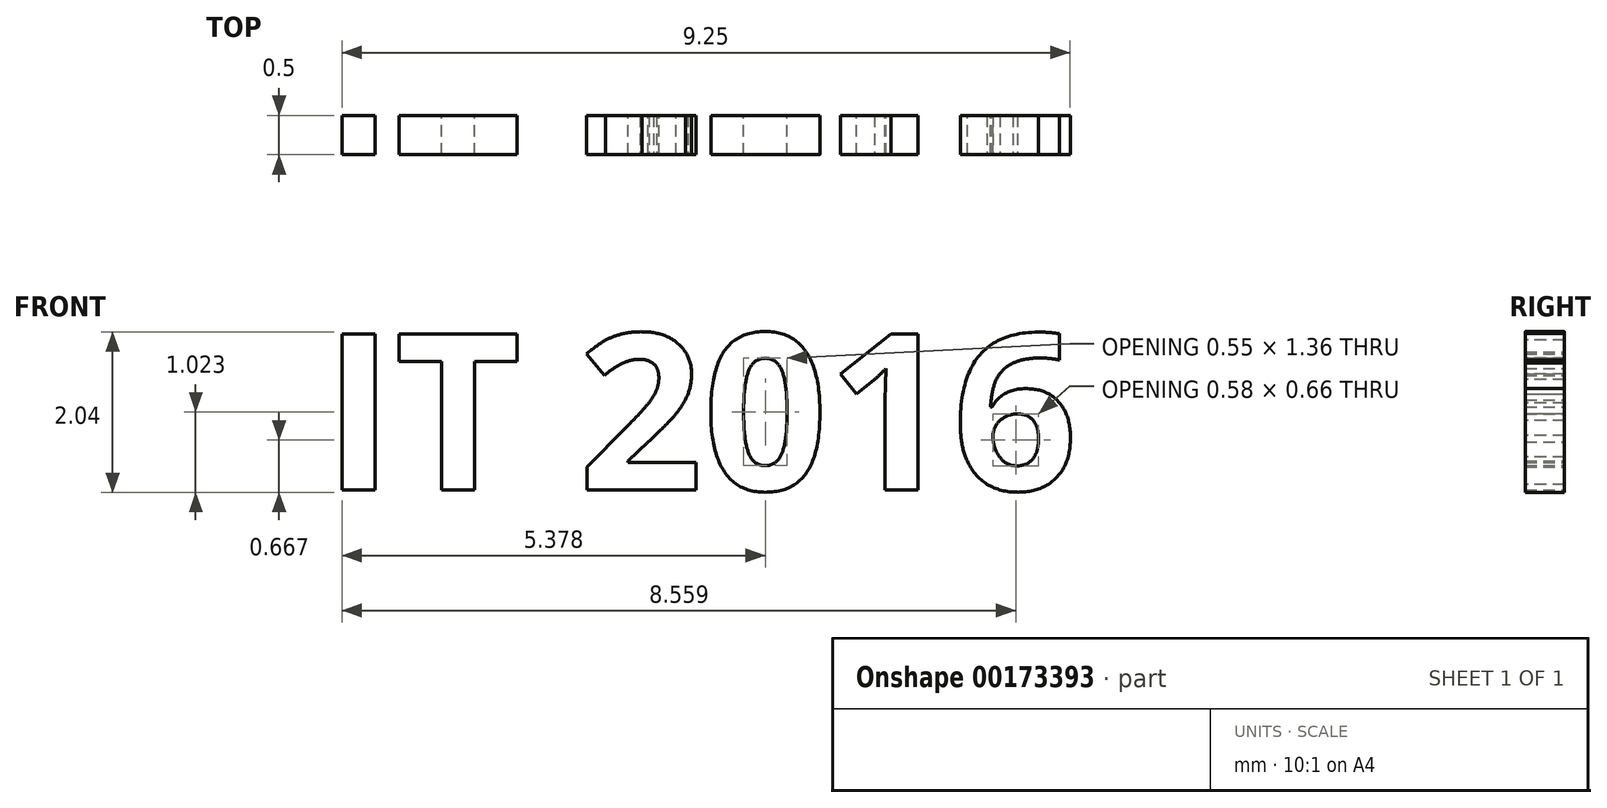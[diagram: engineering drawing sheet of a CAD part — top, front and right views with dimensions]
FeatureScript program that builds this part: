
annotation { "Feature Type Name" : "Feature", "Feature Type Description" : "" }
export const myFeature = defineFeature(function(context is Context, id is Id, definition is map)
    precondition{}
    {
        {
            var Q0;
            Q0=qCreatedBy(makeId("Front.planeOp"),FACE);
            var sketch = newSketch(context, id + "F0", { "sketchPlane" : qUnion([Q0])});
            skText(sketch, "E0", { "text": "IT 2016\n", "fontName": "OpenSans-Bold.ttf"});
            const initialGuessF0  = {"E0": [0, 0, 1, 0, 0.002]};
            skSetInitialGuess(sketch, initialGuessF0);
            skSolve(sketch);
        }
        {
            var Q0;
            Q0 = qSketchRegion(id + "F0", true);
            extrude(context, id + "F1", {"entities" : qUnion([Q0]), "depth" : 0.5 * mm});
        }
    });
